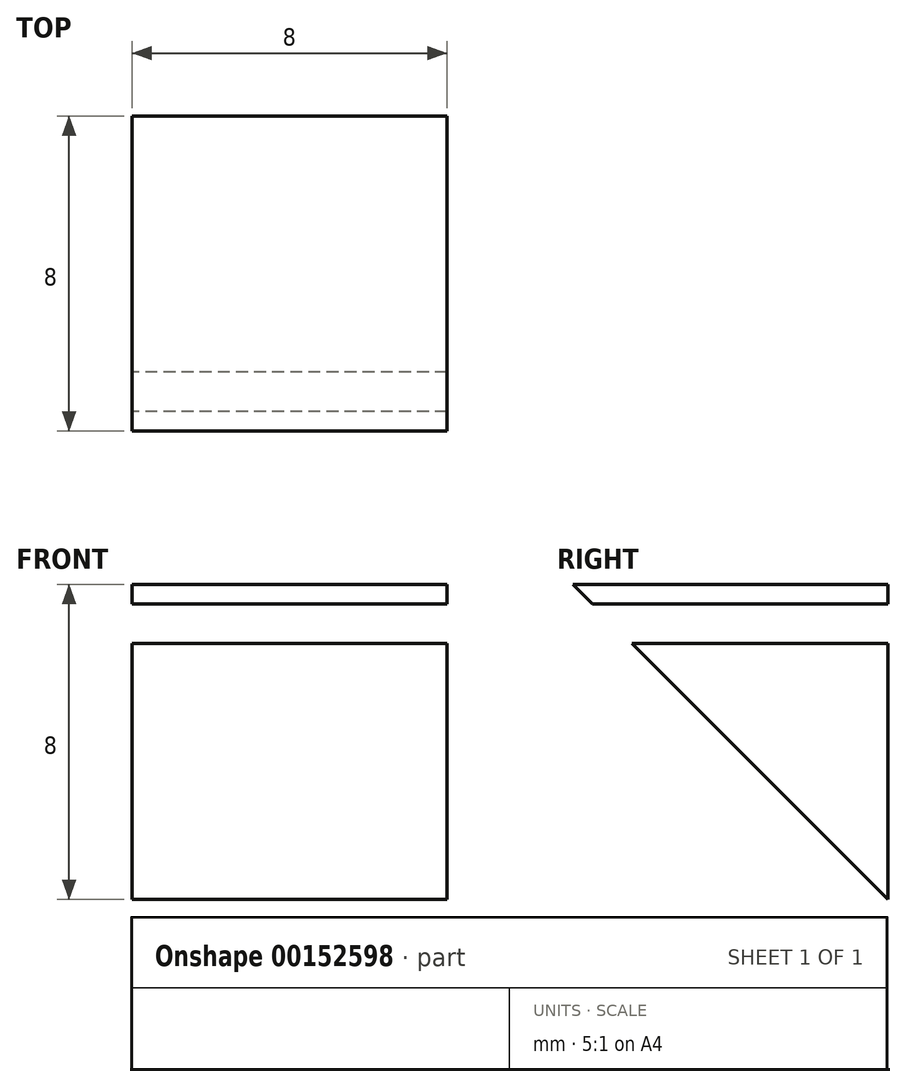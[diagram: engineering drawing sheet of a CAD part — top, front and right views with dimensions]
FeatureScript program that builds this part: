
annotation { "Feature Type Name" : "Feature", "Feature Type Description" : "" }
export const myFeature = defineFeature(function(context is Context, id is Id, definition is map)
    precondition{}
    {
        {
            var Q0;
            Q0=qCreatedBy(makeId("Right.planeOp"),FACE);
            var sketch = newSketch(context, id + "F0", { "sketchPlane" : qUnion([Q0])});
            skLineSegment(sketch, "E0.bottom", {"start": v(-4, 4) * mm, "end": v(4, 4) * mm});
            skLineSegment(sketch, "E0.top", {"start": v(-4, -4) * mm, "end": v(4, -4) * mm});
            skLineSegment(sketch, "E0.left", {"start": v(-4, 4) * mm, "end": v(-4, -4) * mm});
            skLineSegment(sketch, "E0.right", {"start": v(4, 4) * mm, "end": v(4, -4) * mm});
            skPoint(sketch, "E0.middle", {"position": v(0, 0) * mm});
            skLineSegment(sketch, "E1", {"start": v(-4, 4) * mm, "end": v(4, -4) * mm});
            skSolve(sketch);
        }
        {
            var Q0;
            Q0=makeQuery(id+"F0.imprint","IMPRINT",FACE,{"disambiguationData":[TD([[makeQuery(id+"F0.imprint","IMPRINT",EDGE,{"derivedFrom":sQuery(id+"F0.wireOp",EDGE,"E0.bottom")}),-1.0]])]});
            extrude(context, id + "F1", {"entities" : qUnion([Q0]), "endBound" : BoundingType.SYMMETRIC, "depth" : 8 * mm});
        }
        {
            var Q0;
            Q0=makeQuery(id+"F1.opExtrude","SWEPT_FACE",FACE,{"disambiguationData":[OSD([sQuery(id+"F0.wireOp",EDGE,"E0.right")])]});
            var sketch = newSketch(context, id + "F2", { "sketchPlane" : qUnion([Q0])});
            skLineSegment(sketch, "E2.bottom", {"start": v(-4, 3.5) * mm, "end": v(4, 3.5) * mm});
            skLineSegment(sketch, "E2.top", {"start": v(-4, 2.5) * mm, "end": v(4, 2.5) * mm});
            skLineSegment(sketch, "E2.left", {"start": v(-4, 3.5) * mm, "end": v(-4, 2.5) * mm});
            skLineSegment(sketch, "E2.right", {"start": v(4, 3.5) * mm, "end": v(4, 2.5) * mm});
            skPoint(sketch, "E2.middle", {"position": v(0, 3) * mm});
            skSolve(sketch);
        }
        {
            var Q0;
            Q0=makeQuery(id+"F2.imprint","IMPRINT",FACE,{"disambiguationData":[TD([[makeQuery(id+"F2.imprint","IMPRINT",EDGE,{"derivedFrom":sQuery(id+"F2.wireOp",EDGE,"E2.bottom")}),-1.0]])]});
            extrude(context, id + "F3", {"entities" : qUnion([Q0]), "operationType" : NewBodyOperationType.REMOVE, "oppositeDirection" : true, "depth" : 25 * mm});
        }
    });
